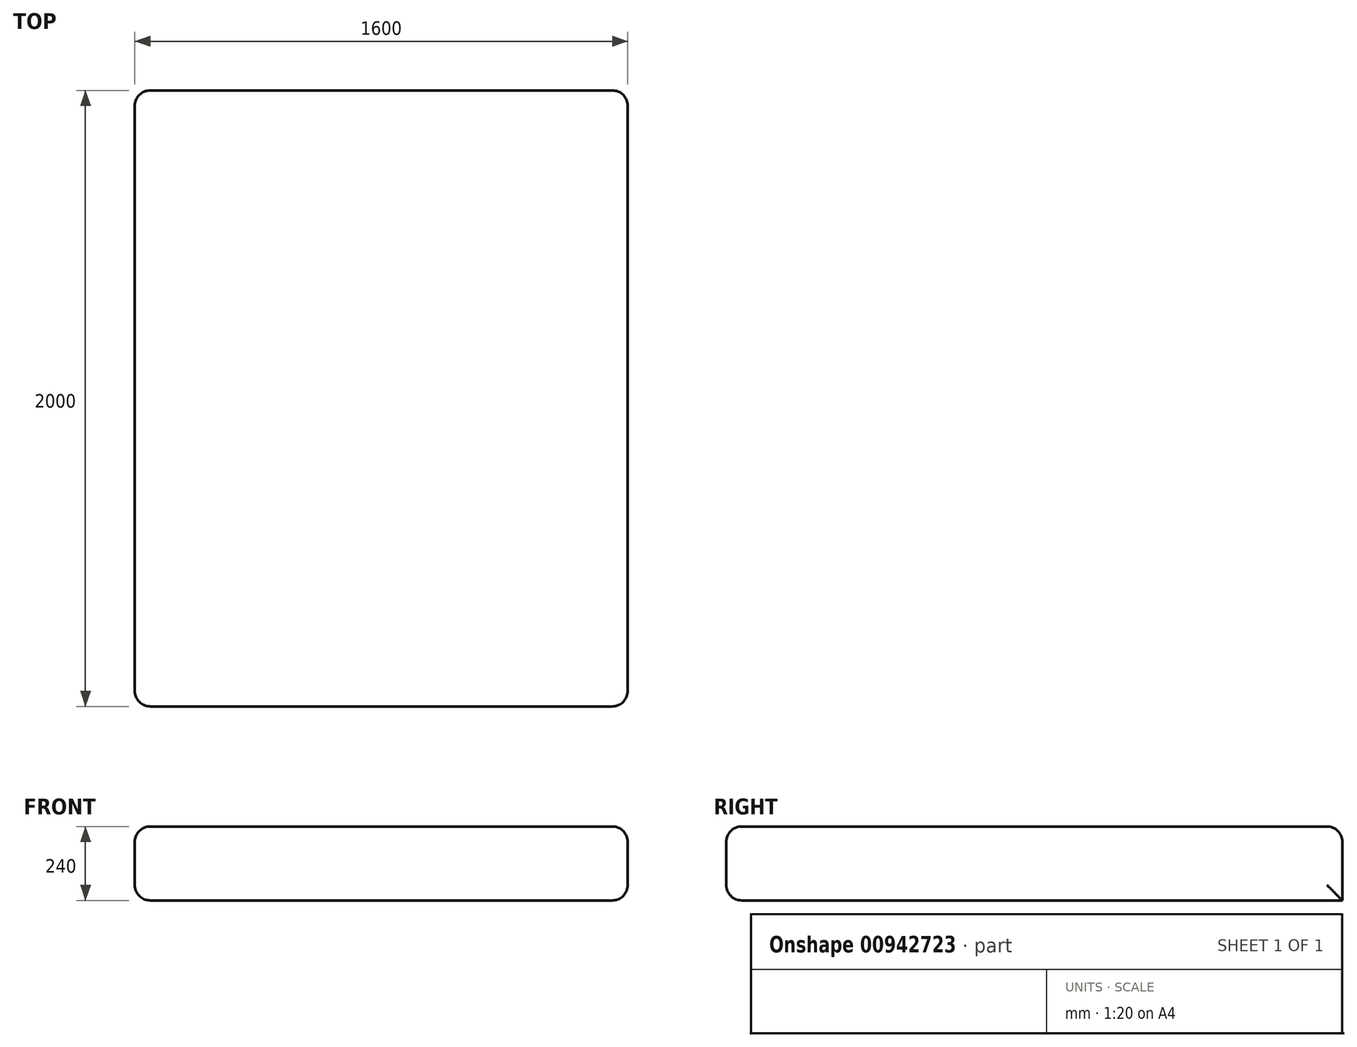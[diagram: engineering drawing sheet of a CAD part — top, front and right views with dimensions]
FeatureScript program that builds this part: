
annotation { "Feature Type Name" : "Feature", "Feature Type Description" : "" }
export const myFeature = defineFeature(function(context is Context, id is Id, definition is map)
    precondition{}
    {
        {
            var Q0;
            Q0=qCreatedBy(makeId("Top.planeOp"),FACE);
            var sketch = newSketch(context, id + "F0", { "sketchPlane" : qUnion([Q0])});
            skLineSegment(sketch, "E0.bottom", {"start": v(800, 1000) * mm, "end": v(-800, 1000) * mm});
            skLineSegment(sketch, "E0.top", {"start": v(800, -1000) * mm, "end": v(-800, -1000) * mm});
            skLineSegment(sketch, "E0.left", {"start": v(800, 1000) * mm, "end": v(800, -1000) * mm});
            skLineSegment(sketch, "E0.right", {"start": v(-800, 1000) * mm, "end": v(-800, -1000) * mm});
            skLineSegment(sketch, "E1", {"start": v(-800, 0) * mm, "end": v(0, 0) * mm, "construction": true});
            skLineSegment(sketch, "E2", {"start": v(0, 0) * mm, "end": v(800, 0) * mm, "construction": true});
            skLineSegment(sketch, "E3", {"start": v(0, -1000) * mm, "end": v(0, 0) * mm, "construction": true});
            skLineSegment(sketch, "E4", {"start": v(0, 0) * mm, "end": v(0, 1000) * mm, "construction": true});
            skSolve(sketch);
        }
        {
            var Q0;
            Q0=makeQuery(id+"F0.imprint","IMPRINT",FACE,{"disambiguationData":[TD([[makeQuery(id+"F0.imprint","IMPRINT",EDGE,{"derivedFrom":sQuery(id+"F0.wireOp",EDGE,"E0.bottom")}),1.0]])]});
            extrude(context, id + "F1", {"entities" : qUnion([Q0]), "depth" : 240 * mm, "offsetDistance" : 25 * mm});
        }
        {
            var Q0;
            Q0=makeQuery(id+"F1.opExtrude","CAP_FACE",FACE,{"disambiguationData":[OSD([sQuery(id+"F0.wireOp",EDGE,"E0.bottom"),sQuery(id+"F0.wireOp",EDGE,"E0.top"),sQuery(id+"F0.wireOp",EDGE,"E0.left"),sQuery(id+"F0.wireOp",EDGE,"E0.right")])],"isStart":false});
            var Q1;
            Q1=makeQuery(id+"F1.opExtrude","SWEPT_EDGE",EDGE,{"disambiguationData":[OSD([sQuery(id+"F0.wireOp",EDGE,"E0.top"),sQuery(id+"F0.wireOp",EDGE,"E0.left")])]});
            var Q2;
            Q2=makeQuery(id+"F1.opExtrude","SWEPT_EDGE",EDGE,{"disambiguationData":[OSD([sQuery(id+"F0.wireOp",EDGE,"E0.bottom"),sQuery(id+"F0.wireOp",EDGE,"E0.left")])]});
            var Q3;
            Q3=makeQuery(id+"F1.opExtrude","SWEPT_EDGE",EDGE,{"disambiguationData":[OSD([sQuery(id+"F0.wireOp",EDGE,"E0.top"),sQuery(id+"F0.wireOp",EDGE,"E0.right")])]});
            var Q4;
            Q4=makeQuery(id+"F1.opExtrude","SWEPT_EDGE",EDGE,{"disambiguationData":[OSD([sQuery(id+"F0.wireOp",EDGE,"E0.bottom"),sQuery(id+"F0.wireOp",EDGE,"E0.right")])]});
            var Q5;
            Q5=makeQuery(id+"F1.opExtrude","CAP_EDGE",EDGE,{"disambiguationData":[OSD([sQuery(id+"F0.wireOp",EDGE,"E0.top")])],"isStart":true});
            var Q6;
            Q6=makeQuery(id+"F1.opExtrude","CAP_EDGE",EDGE,{"disambiguationData":[OSD([sQuery(id+"F0.wireOp",EDGE,"E0.right")])],"isStart":true});
            var Q7;
            Q7=makeQuery(id+"F1.opExtrude","CAP_EDGE",EDGE,{"disambiguationData":[OSD([sQuery(id+"F0.wireOp",EDGE,"E0.left")])],"isStart":true});
            fillet(context, id + "F2", {"entities" : qUnion([Q0, Q1, Q2, Q3, Q4, Q5, Q6, Q7]), "radius" : 50 * mm, "tangentPropagation" : true, "allowEdgeOverflow" : false});
        }
    });
